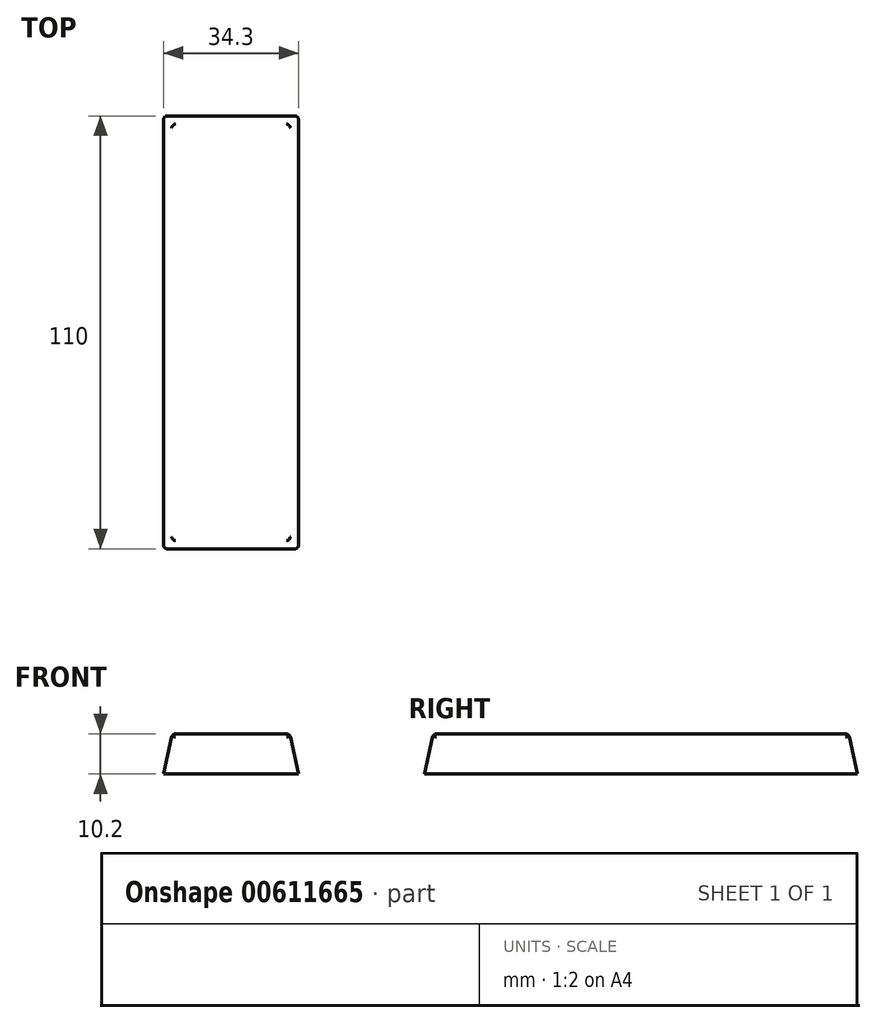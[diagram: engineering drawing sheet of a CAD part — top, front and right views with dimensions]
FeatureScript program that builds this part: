
annotation { "Feature Type Name" : "Feature", "Feature Type Description" : "" }
export const myFeature = defineFeature(function(context is Context, id is Id, definition is map)
    precondition{}
    {
        {
            var Q0;
            Q0=qCreatedBy(makeId("Top.planeOp"),FACE);
            var sketch = newSketch(context, id + "F0", { "sketchPlane" : qUnion([Q0])});
            skLineSegment(sketch, "E0.bottom", {"start": v(17.15, -55) * mm, "end": v(-17.15, -55) * mm});
            skLineSegment(sketch, "E0.top", {"start": v(17.15, 55) * mm, "end": v(-17.15, 55) * mm});
            skLineSegment(sketch, "E0.left", {"start": v(17.15, -55) * mm, "end": v(17.15, 55) * mm});
            skLineSegment(sketch, "E0.right", {"start": v(-17.15, -55) * mm, "end": v(-17.15, 55) * mm});
            skSolve(sketch);
        }
        {
            var Q0;
            Q0 = qSketchRegion(id + "F0", true);
            extrude(context, id + "F1", {"entities" : qUnion([Q0]), "depth" : 10.2 * mm, "offsetDistance" : 25 * mm, "hasDraft" : true, "draftAngle" : 12.5 * degree, "draftPullDirection" : true});
        }
        {
            var Q0;
            Q0=makeQuery(id+"F1.opExtrude","CAP_FACE",FACE,{"disambiguationData":[OSD([sQuery(id+"F0.wireOp",EDGE,"E0.bottom"),sQuery(id+"F0.wireOp",EDGE,"E0.top"),sQuery(id+"F0.wireOp",EDGE,"E0.left"),sQuery(id+"F0.wireOp",EDGE,"E0.right")])],"isStart":false});
            var Q1;
            Q1=makeQuery(id+"F1.opExtrude","SWEPT_EDGE",EDGE,{"disambiguationData":[OSD([sQuery(id+"F0.wireOp",EDGE,"E0.top"),sQuery(id+"F0.wireOp",EDGE,"E0.left")])]});
            var Q2;
            Q2=makeQuery(id+"F1.opExtrude","SWEPT_EDGE",EDGE,{"disambiguationData":[OSD([sQuery(id+"F0.wireOp",EDGE,"E0.top"),sQuery(id+"F0.wireOp",EDGE,"E0.right")])]});
            var Q3;
            Q3=makeQuery(id+"F1.opExtrude","SWEPT_EDGE",EDGE,{"disambiguationData":[OSD([sQuery(id+"F0.wireOp",EDGE,"E0.bottom"),sQuery(id+"F0.wireOp",EDGE,"E0.left")])]});
            var Q4;
            Q4=makeQuery(id+"F1.opExtrude","SWEPT_EDGE",EDGE,{"disambiguationData":[OSD([sQuery(id+"F0.wireOp",EDGE,"E0.bottom"),sQuery(id+"F0.wireOp",EDGE,"E0.right")])]});
            fillet(context, id + "F2", {"entities" : qUnion([Q0, Q1, Q2, Q3, Q4]), "radius" : 1 * mm, "tangentPropagation" : true, "allowEdgeOverflow" : false});
        }
    });
